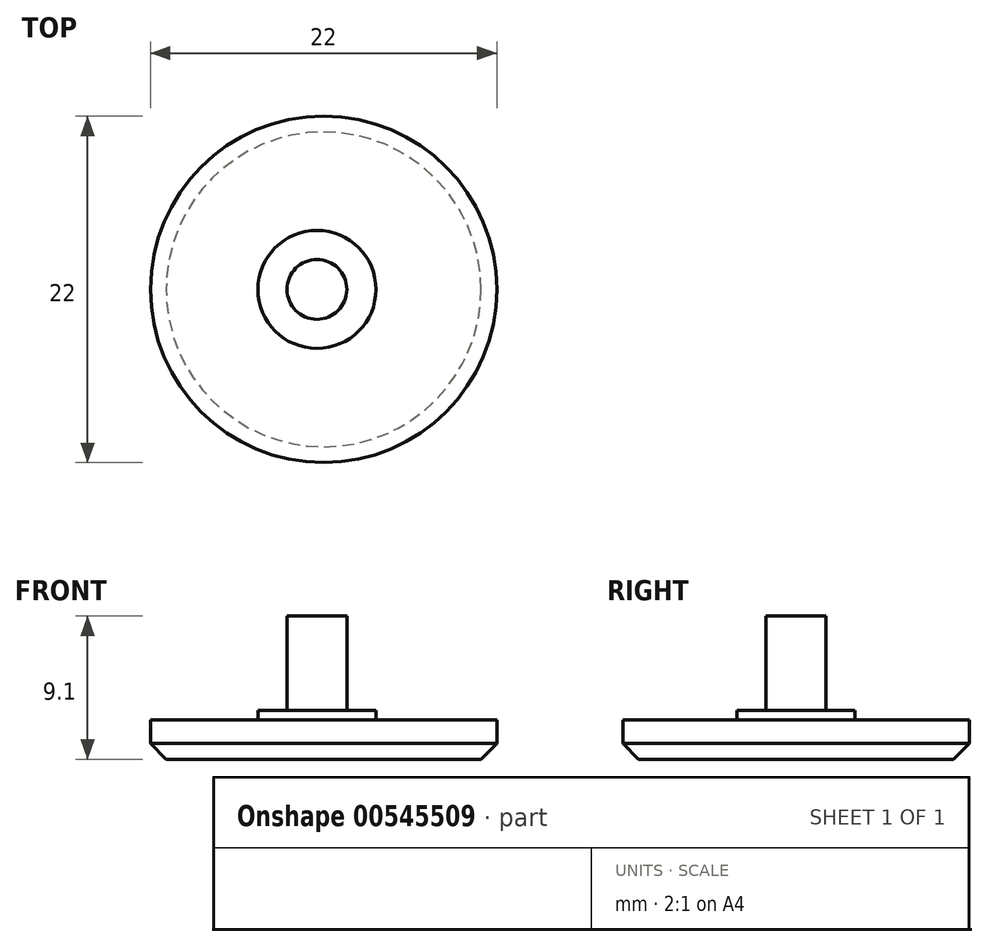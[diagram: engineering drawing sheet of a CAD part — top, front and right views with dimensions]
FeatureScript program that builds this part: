
annotation { "Feature Type Name" : "Feature", "Feature Type Description" : "" }
export const myFeature = defineFeature(function(context is Context, id is Id, definition is map)
    precondition{}
    {
        {
            var Q0;
            Q0=qCreatedBy(makeId("Top.planeOp"),FACE);
            var sketch = newSketch(context, id + "F0", { "sketchPlane" : qUnion([Q0])});
            skCircle(sketch, "E0", {"center": v(0.43, 0) * mm, "radius": 11 * mm});
            skSolve(sketch);
        }
        {
            var Q0;
            Q0=makeQuery(id+"F0.imprint","IMPRINT",FACE,{"disambiguationData":[TD([[makeQuery(id+"F0.imprint","IMPRINT",EDGE,{"derivedFrom":sQuery(id+"F0.wireOp",EDGE,"E0")}),1.0]])]});
            extrude(context, id + "F1", {"entities" : qUnion([Q0]), "depth" : 2.5 * mm, "offsetDistance" : 25 * mm});
        }
        {
            var Q0;
            Q0=makeQuery(id+"F1.opExtrude","CAP_EDGE",EDGE,{"disambiguationData":[OSD([sQuery(id+"F0.wireOp",EDGE,"E0")])],"isStart":true});
            chamfer(context, id + "F2", {"entities" : qUnion([Q0]), "chamferType" : ChamferType.OFFSET_ANGLE, "width" : 1 * mm, "oppositeDirection" : false, "angle" : 45 * degree, "tangentPropagation" : true});
        }
        {
            var Q0;
            Q0=makeQuery(id+"F1.opExtrude","CAP_FACE",FACE,{"disambiguationData":[OSD([sQuery(id+"F0.wireOp",EDGE,"E0")])],"isStart":false});
            var sketch = newSketch(context, id + "F3", { "sketchPlane" : qUnion([Q0])});
            skCircle(sketch, "E1", {"center": v(0, 0) * mm, "radius": 3.75 * mm});
            skSolve(sketch);
        }
        {
            var Q0;
            Q0=makeQuery(id+"F3.imprint","IMPRINT",FACE,{"disambiguationData":[TD([[makeQuery(id+"F3.imprint","IMPRINT",EDGE,{"derivedFrom":sQuery(id+"F3.wireOp",EDGE,"E1")}),1.0]])]});
            extrude(context, id + "F4", {"entities" : qUnion([Q0]), "operationType" : NewBodyOperationType.ADD, "depth" : .6 * mm, "offsetDistance" : 25 * mm});
        }
        {
            var Q0;
            Q0=makeQuery(id+"F4.opExtrude","CAP_FACE",FACE,{"disambiguationData":[OSD([sQuery(id+"F3.wireOp",EDGE,"E1")])],"isStart":false});
            var sketch = newSketch(context, id + "F5", { "sketchPlane" : qUnion([Q0])});
            skCircle(sketch, "E2", {"center": v(0, 0) * mm, "radius": 1.9 * mm});
            skSolve(sketch);
        }
        {
            var Q0;
            Q0=makeQuery(id+"F5.imprint","IMPRINT",FACE,{"disambiguationData":[TD([[makeQuery(id+"F5.imprint","IMPRINT",EDGE,{"derivedFrom":sQuery(id+"F5.wireOp",EDGE,"E2")}),1.0]])]});
            extrude(context, id + "F6", {"entities" : qUnion([Q0]), "operationType" : NewBodyOperationType.ADD, "depth" : 6 * mm, "offsetDistance" : 25 * mm});
        }
    });
